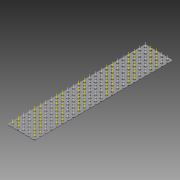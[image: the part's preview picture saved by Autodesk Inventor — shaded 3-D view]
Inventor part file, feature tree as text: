
AUTODESK INVENTOR PART (.ipt)
format: ipt  version: 2015 (Build 190159000, 159)  size: 1,323,008 bytes
history: native  units: in
note: dims shown in document units (in); Inventor stores cm internally (conversion verified against a paired STEP export)
features: other x134, extrude x2, pattern_linear x1, imported_body x1
ambient origin geometry x8: Origin, YZ Plane, XZ Plane, XY Plane, X Axis, Y Axis, Z Axis, Center Point
bodies: Body1 (feature_tree)
feature tree (138):
  other  "Diamond-Pattern"
  other  "Plate"
  extrude  "length cut"  TaperAngle=0.0deg  [1 undecoded]
  extrude  "width cut"  TaperAngle=0.0deg  [1 undecoded]
  other  "constraint axis"
  pattern_linear  "constraint axes"  Spacing1=0.5in  [1 undecoded]
  other  "front plane"
  other  "right plane"
  imported_body  "Base1"
  other  "length profile"
  other  "width profile"
  other  "Work Point1"
  other  "Work Axis36"
  other  "Work Axis37"
  other  "Work Axis38"
  other  "Work Axis39"
  other  "Work Axis40"
  other  "Work Axis41"
  other  "Work Axis42"
  other  "Work Axis43"
  other  "Work Axis44"
  other  "Work Axis45"
  other  "Work Axis46"
  other  "Work Axis47"
  other  "Work Axis48"
  other  "Work Axis49"
  other  "Work Axis50"
  other  "Work Axis51"
  other  "Work Axis52"
  other  "Work Axis53"
  other  "Work Axis54"
  other  "Work Axis55"
  other  "Work Axis56"
  other  "Work Axis57"
  other  "Work Axis58"
  other  "Work Axis59"
  other  "Work Axis60"
  other  "Work Axis61"
  other  "Work Axis62"
  other  "Work Axis63"
  other  "Work Axis64"
  other  "back plane"
  other  "left plane"
  other  "Work Axis75"
  other  "Work Axis76"
  other  "Work Axis77"
  other  "Work Axis78"
  other  "Work Axis79"
  other  "Work Axis80"
  other  "Work Axis81"
  other  "Work Axis82"
  other  "Work Axis83"
  other  "Work Axis84"
  other  "Work Axis85"
  other  "Work Axis86"
  other  "Work Axis87"
  other  "Work Axis88"
  other  "Work Axis89"
  other  "Work Axis90"
  other  "Work Axis91"
  other  "Work Axis92"
  other  "Work Axis93"
  other  "Work Axis94"
  other  "Work Axis95"
  other  "Work Axis96"
  other  "Work Axis97"
  other  "Work Axis98"
  other  "Work Axis99"
  other  "Work Axis100"
  other  "Work Axis101"
  other  "Work Axis102"
  other  "Work Axis103"
  other  "Work Axis104"
  other  "Work Axis105"
  other  "Work Axis106"
  other  "Work Axis107"
  other  "Work Axis108"
  other  "Work Axis109"
  other  "Work Axis110"
  other  "Work Axis111"
  other  "Work Axis112"
  other  "Work Axis113"
  other  "Work Axis114"
  other  "Work Axis115"
  other  "Work Axis116"
  other  "Work Axis117"
  other  "Work Axis118"
  other  "Work Axis119"
  other  "Work Axis120"
  other  "Work Axis121"
  other  "Work Axis122"
  other  "Work Axis123"
  other  "Work Axis124"
  other  "Work Axis125"
  other  "Work Axis126"
  other  "Work Axis127"
  other  "Work Axis128"
  other  "Work Axis129"
  other  "Work Axis130"
  other  "Work Axis131"
  other  "Work Axis132"
  other  "Work Axis133"
  other  "Work Axis134"
  other  "Work Axis135"
  other  "Work Axis136"
  other  "Work Axis137"
  other  "Work Axis138"
  other  "Work Axis139"
  other  "Work Axis140"
  other  "Work Axis141"
  other  "Work Axis142"
  other  "Work Axis143"
  other  "Work Axis144"
  other  "Work Axis145"
  other  "Work Axis146"
  other  "Work Axis147"
  other  "Work Axis148"
  other  "Work Axis149"
  other  "Work Axis150"
  other  "Work Axis151"
  other  "Work Axis152"
  other  "Work Axis153"
  other  "Work Axis154"
  other  "Work Axis155"
  other  "Work Axis156"
  other  "Work Axis157"
  other  "Work Axis158"
  other  "Work Axis159"
  other  "Work Axis160"
  other  "Work Axis161"
  other  "Work Axis162"
  other  "Work Axis163"
  other  "Work Axis164"
  other  "Work Axis165"
  other  "Work Axis166"
  other  "Work Axis167"
  other  "Work Axis168"
  other  "Work Axis169"
note: 3 required parameter values undecoded (feature->parameter linkage not recoverable at this tier; creation-order binding heuristic only, values carry confidence <= 0.55)
